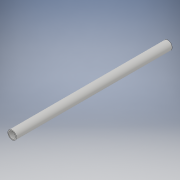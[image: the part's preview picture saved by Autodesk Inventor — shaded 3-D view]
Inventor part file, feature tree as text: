
AUTODESK INVENTOR PART (.ipt)
format: ipt  version: 2019 (Build 230136000, 136)  size: 95,744 bytes
history: native  units: mm
features: extrude x1, plane x1, sketch x1
ambient origin geometry x8: Origin, YZ Plane, XZ Plane, XY Plane, X Axis, Y Axis, Z Axis, Center Point
bodies: Solid1 (feature_tree)
feature tree (3):
  extrude  "Extrusion1"  Depth=270.0mm
  plane  "Work Plane1"
  sketch  "Sketch1"  dims[d0=15.0mm d1=12.0mm d2=270.0mm d3=0.0mm d4=-135.0mm]
